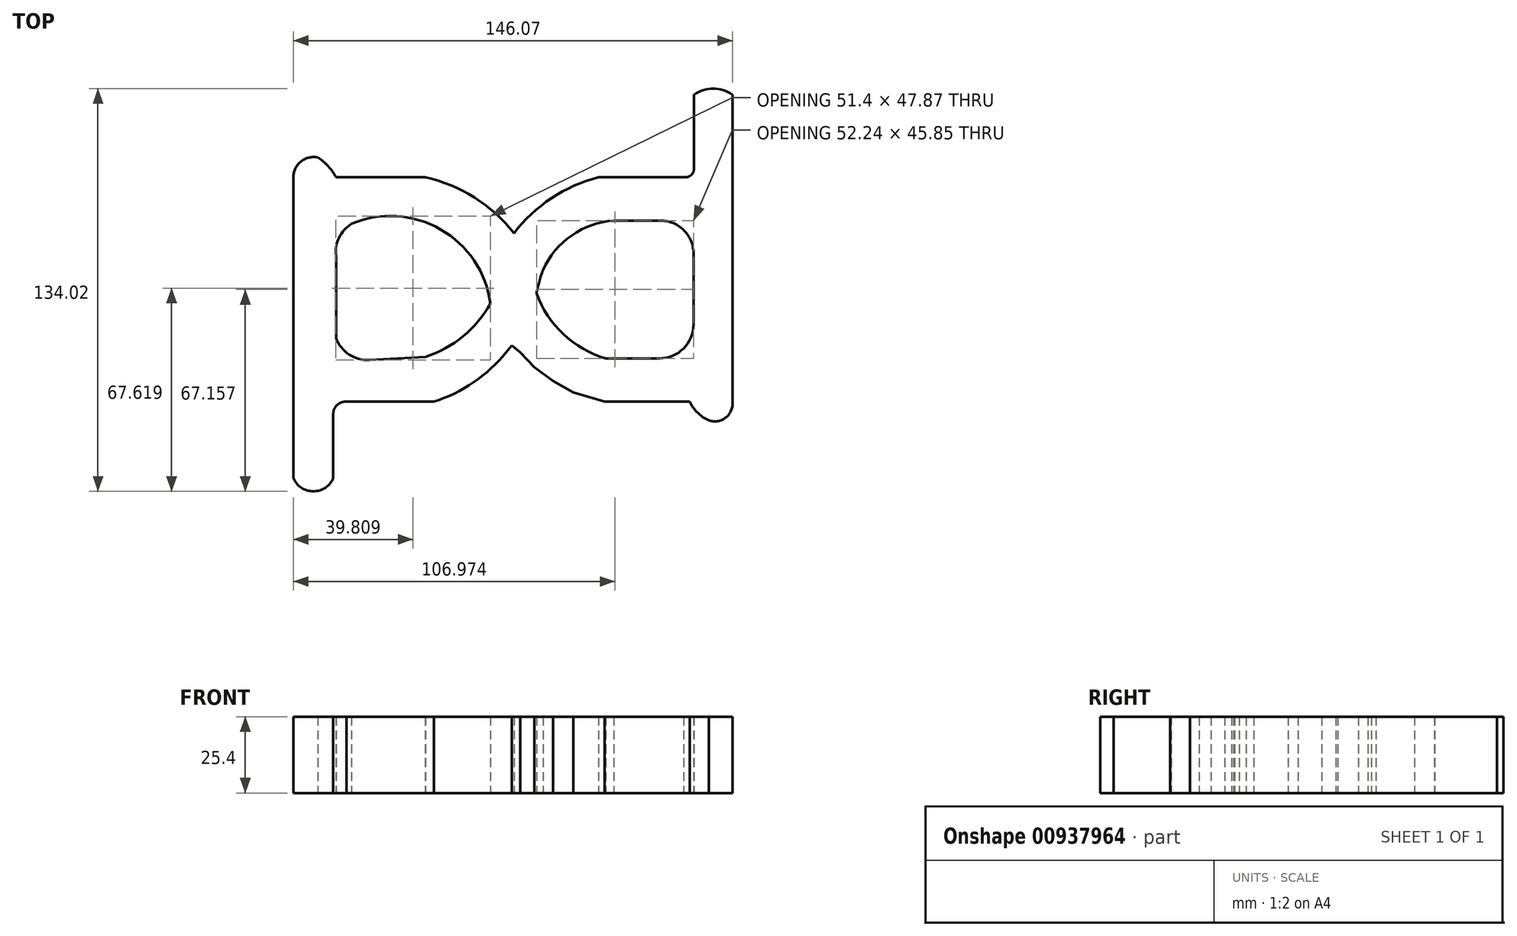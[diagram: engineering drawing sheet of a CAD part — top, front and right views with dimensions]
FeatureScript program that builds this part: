
annotation { "Feature Type Name" : "Feature", "Feature Type Description" : "" }
export const myFeature = defineFeature(function(context is Context, id is Id, definition is map)
    precondition{}
    {
        {
            var Q0;
            Q0=qCreatedBy(makeId("Top.planeOp"),FACE);
            var sketch = newSketch(context, id + "F0", { "sketchPlane" : qUnion([Q0])});
            skLineSegment(sketch, "E0", {"start": v(-113.45, -20.43) * mm, "end": v(-113.45, -120.53) * mm});
            skArc(sketch, "E1", {"start": v(-113.45, -120.53) * mm, "mid": v(-106.81, -124.94) * mm, "end": v(-100.18, -120.53) * mm});
            skLineSegment(sketch, "E2", {"start": v(-100.18, -120.53) * mm, "end": v(-100.18, -99.16) * mm});
            skArc(sketch, "E3", {"start": v(-95.8, -95.14) * mm, "mid": v(-98.87, -96.18) * mm, "end": v(-100.18, -99.16) * mm});
            skLineSegment(sketch, "E4", {"start": v(-95.8, -95.14) * mm, "end": v(-66.75, -95.14) * mm});
            skArc(sketch, "E5", {"start": v(-66.75, -95.14) * mm, "mid": v(-53.5, -88.66) * mm, "end": v(-42.64, -78.7) * mm});
            skLineSegment(sketch, "E6", {"start": v(-42.64, -78.7) * mm, "end": v(-40.77, -76.4) * mm});
            skLineSegment(sketch, "E7", {"start": v(-40.77, -76.4) * mm, "end": v(-37.95, -78.7) * mm});
            skLineSegment(sketch, "E8", {"start": v(-37.95, -78.7) * mm, "end": v(-33.33, -83.63) * mm});
            skLineSegment(sketch, "E9", {"start": v(-33.33, -83.63) * mm, "end": v(-27.12, -88.2) * mm});
            skLineSegment(sketch, "E10", {"start": v(-27.12, -88.2) * mm, "end": v(-20.36, -92.03) * mm});
            skLineSegment(sketch, "E11", {"start": v(-20.36, -92.03) * mm, "end": v(-9.95, -95.14) * mm});
            skLineSegment(sketch, "E12", {"start": v(-9.95, -95.14) * mm, "end": v(-1.54, -95.14) * mm});
            skLineSegment(sketch, "E13", {"start": v(-1.54, -95.14) * mm, "end": v(11.6, -95.14) * mm});
            skLineSegment(sketch, "E14", {"start": v(11.6, -95.14) * mm, "end": v(18.37, -95.14) * mm});
            skArc(sketch, "E15", {"start": v(18.37, -95.14) * mm, "mid": v(21, -98.82) * mm, "end": v(24.76, -101.35) * mm});
            skArc(sketch, "E16", {"start": v(24.76, -101.35) * mm, "mid": v(30.38, -100.39) * mm, "end": v(32.59, -95.14) * mm});
            skLineSegment(sketch, "E17", {"start": v(32.59, -83.26) * mm, "end": v(32.59, -36.87) * mm});
            skLineSegment(sketch, "E18", {"start": v(32.59, -36.87) * mm, "end": v(32.59, 6.97) * mm});
            skArc(sketch, "E19", {"start": v(32.59, 6.97) * mm, "mid": v(26.2, 9.08) * mm, "end": v(19.83, 6.97) * mm});
            skLineSegment(sketch, "E20", {"start": v(19.83, 6.97) * mm, "end": v(19.83, -17.5) * mm});
            skArc(sketch, "E21", {"start": v(16.36, -20.43) * mm, "mid": v(18.77, -19.77) * mm, "end": v(19.83, -17.5) * mm});
            skLineSegment(sketch, "E22", {"start": v(16.36, -20.43) * mm, "end": v(-11.96, -20.43) * mm});
            skArc(sketch, "E23", {"start": v(-11.96, -20.43) * mm, "mid": v(-27.6, -27.37) * mm, "end": v(-40.09, -39.06) * mm});
            skArc(sketch, "E24", {"start": v(-40.09, -39.06) * mm, "mid": v(-53.26, -27.16) * mm, "end": v(-69.68, -20.43) * mm});
            skLineSegment(sketch, "E25", {"start": v(-69.68, -20.43) * mm, "end": v(-99.27, -20.43) * mm});
            skArc(sketch, "E26", {"start": v(-99.27, -20.43) * mm, "mid": v(-101.86, -16.76) * mm, "end": v(-105.3, -13.85) * mm});
            skArc(sketch, "E27", {"start": v(-105.3, -13.85) * mm, "mid": v(-110.94, -15.2) * mm, "end": v(-113.45, -20.43) * mm});
            skArc(sketch, "E28", {"start": v(-47.94, -62.44) * mm, "mid": v(-64.5, -37.76) * mm, "end": v(-94.15, -35.95) * mm});
            skArc(sketch, "E29", {"start": v(-94.15, -35.95) * mm, "mid": v(-98.26, -40.5) * mm, "end": v(-99.27, -46.55) * mm});
            skLineSegment(sketch, "E30", {"start": v(-99.27, -46.55) * mm, "end": v(-99.27, -73.95) * mm});
            skArc(sketch, "E31", {"start": v(-99.27, -73.95) * mm, "mid": v(-94.9, -79.44) * mm, "end": v(-88.13, -81.25) * mm});
            skLineSegment(sketch, "E32", {"start": v(-88.13, -81.25) * mm, "end": v(-69.5, -80.22) * mm});
            skArc(sketch, "E33", {"start": v(-69.5, -80.22) * mm, "mid": v(-57.04, -73.37) * mm, "end": v(-47.94, -62.44) * mm});
            skArc(sketch, "E34", {"start": v(-6.84, -34.86) * mm, "mid": v(-20.9, -39.8) * mm, "end": v(-30.4, -51.3) * mm});
            skLineSegment(sketch, "E35", {"start": v(-6.84, -34.86) * mm, "end": v(8.69, -34.86) * mm});
            skArc(sketch, "E36", {"start": v(19.65, -46) * mm, "mid": v(16.5, -38.13) * mm, "end": v(8.69, -34.86) * mm});
            skLineSegment(sketch, "E37", {"start": v(19.65, -46) * mm, "end": v(19.65, -69.38) * mm});
            skArc(sketch, "E38", {"start": v(8.32, -80.7) * mm, "mid": v(16.33, -77.39) * mm, "end": v(19.65, -69.38) * mm});
            skLineSegment(sketch, "E39", {"start": v(8.32, -80.7) * mm, "end": v(-9.58, -80.7) * mm});
            skArc(sketch, "E40", {"start": v(-32.6, -59.15) * mm, "mid": v(-23.64, -72.66) * mm, "end": v(-9.58, -80.7) * mm});
            skArc(sketch, "E41", {"start": v(-30.4, -51.3) * mm, "mid": v(-31.7, -55.17) * mm, "end": v(-32.6, -59.15) * mm});
            skLineSegment(sketch, "E42", {"start": v(32.59, -95.14) * mm, "end": v(32.59, -83.26) * mm});
            skSolve(sketch);
        }
        {
            var Q0;
            Q0=sQuery(id+"F0.wireOp",EDGE,"E25");
            var Q1;
            Q1=sQuery(id+"F0.wireOp",EDGE,"E26");
            var Q2;
            Q2=sQuery(id+"F0.wireOp",EDGE,"E27");
            var Q3;
            Q3=sQuery(id+"F0.wireOp",EDGE,"E0");
            var Q4;
            Q4=sQuery(id+"F0.wireOp",EDGE,"E24");
            var Q5;
            Q5=sQuery(id+"F0.wireOp",EDGE,"E23");
            var Q6;
            Q6=sQuery(id+"F0.wireOp",EDGE,"E22");
            var Q7;
            Q7=sQuery(id+"F0.wireOp",EDGE,"E20");
            var Q8;
            Q8=sQuery(id+"F0.wireOp",EDGE,"E21");
            var Q9;
            Q9=sQuery(id+"F0.wireOp",EDGE,"E19");
            var Q10;
            Q10=sQuery(id+"F0.wireOp",EDGE,"E18");
            var Q11;
            Q11=sQuery(id+"F0.wireOp",EDGE,"E17");
            var Q12;
            Q12=sQuery(id+"F0.wireOp",EDGE,"E16");
            var Q13;
            Q13=sQuery(id+"F0.wireOp",EDGE,"E14");
            var Q14;
            Q14=sQuery(id+"F0.wireOp",EDGE,"E15");
            var Q15;
            Q15=sQuery(id+"F0.wireOp",EDGE,"E13");
            var Q16;
            Q16=sQuery(id+"F0.wireOp",EDGE,"E12");
            var Q17;
            Q17=sQuery(id+"F0.wireOp",EDGE,"E11");
            var Q18;
            Q18=sQuery(id+"F0.wireOp",EDGE,"E10");
            var Q19;
            Q19=sQuery(id+"F0.wireOp",EDGE,"E9");
            var Q20;
            Q20=sQuery(id+"F0.wireOp",EDGE,"E8");
            var Q21;
            Q21=sQuery(id+"F0.wireOp",EDGE,"E7");
            var Q22;
            Q22=sQuery(id+"F0.wireOp",EDGE,"E6");
            var Q23;
            Q23=sQuery(id+"F0.wireOp",EDGE,"E5");
            var Q24;
            Q24=sQuery(id+"F0.wireOp",EDGE,"E4");
            var Q25;
            Q25=sQuery(id+"F0.wireOp",EDGE,"E3");
            var Q26;
            Q26=sQuery(id+"F0.wireOp",EDGE,"E2");
            var Q27;
            Q27=sQuery(id+"F0.wireOp",EDGE,"E1");
            var Q28;
            Q28=sQuery(id+"F0.wireOp",EDGE,"E42");
            extrude(context, id + "F1", {"bodyType" : ToolBodyType.SURFACE, "surfaceEntities" : qUnion([Q0, Q1, Q2, Q3, Q4, Q5, Q6, Q7, Q8, Q9, Q10, Q11, Q12, Q13, Q14, Q15, Q16, Q17, Q18, Q19, Q20, Q21, Q22, Q23, Q24, Q25, Q26, Q27, Q28]), "depth" : 25.4 * mm, "offsetDistance" : 25.4 * mm});
        }
        {
            var Q0;
            Q0 = qSketchRegion(id + "F0", true);
            extrude(context, id + "F2", {"entities" : qUnion([Q0]), "depth" : 25.4 * mm, "offsetDistance" : 25.4 * mm});
        }
    });
